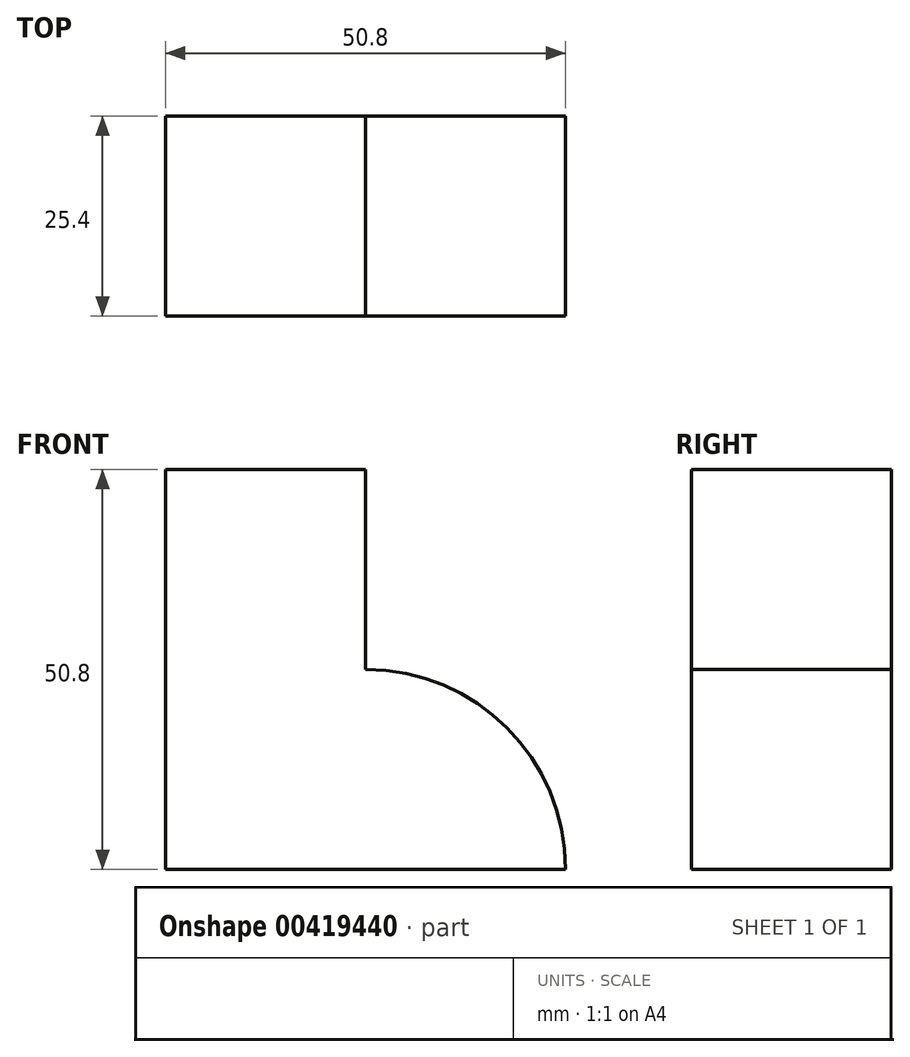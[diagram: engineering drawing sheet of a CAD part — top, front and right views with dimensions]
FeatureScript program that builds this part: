
annotation { "Feature Type Name" : "Feature", "Feature Type Description" : "" }
export const myFeature = defineFeature(function(context is Context, id is Id, definition is map)
    precondition{}
    {
        {
            var Q0;
            Q0=qCreatedBy(makeId("Front.planeOp"),FACE);
            var sketch = newSketch(context, id + "F0", { "sketchPlane" : qUnion([Q0])});
            skLineSegment(sketch, "E0.top", {"start": v(25.4, -25.4) * mm, "end": v(-25.4, -25.4) * mm});
            skLineSegment(sketch, "E0.right", {"start": v(-25.4, 25.4) * mm, "end": v(-25.4, -25.4) * mm});
            skPoint(sketch, "E0.middle", {"position": v(0, 0) * mm});
            skPoint(sketch, "E0.left.start.orphan", {"position": v(25.4, 25.4) * mm});
            skLineSegment(sketch, "E1", {"start": v(-25.4, 25.4) * mm, "end": v(0, 25.4) * mm});
            skLineSegment(sketch, "E2", {"start": v(0, 25.4) * mm, "end": v(0, 0) * mm});
            skArc(sketch, "E3", {"start": v(25.4, -25.4) * mm, "mid": v(17.96, -7.44) * mm, "end": v(0, 0) * mm});
            skSolve(sketch);
        }
        {
            var Q0;
            Q0 = qSketchRegion(id + "F0", true);
            extrude(context, id + "F1", {"entities" : qUnion([Q0]), "depth" : 25.4 * mm});
        }
    });
